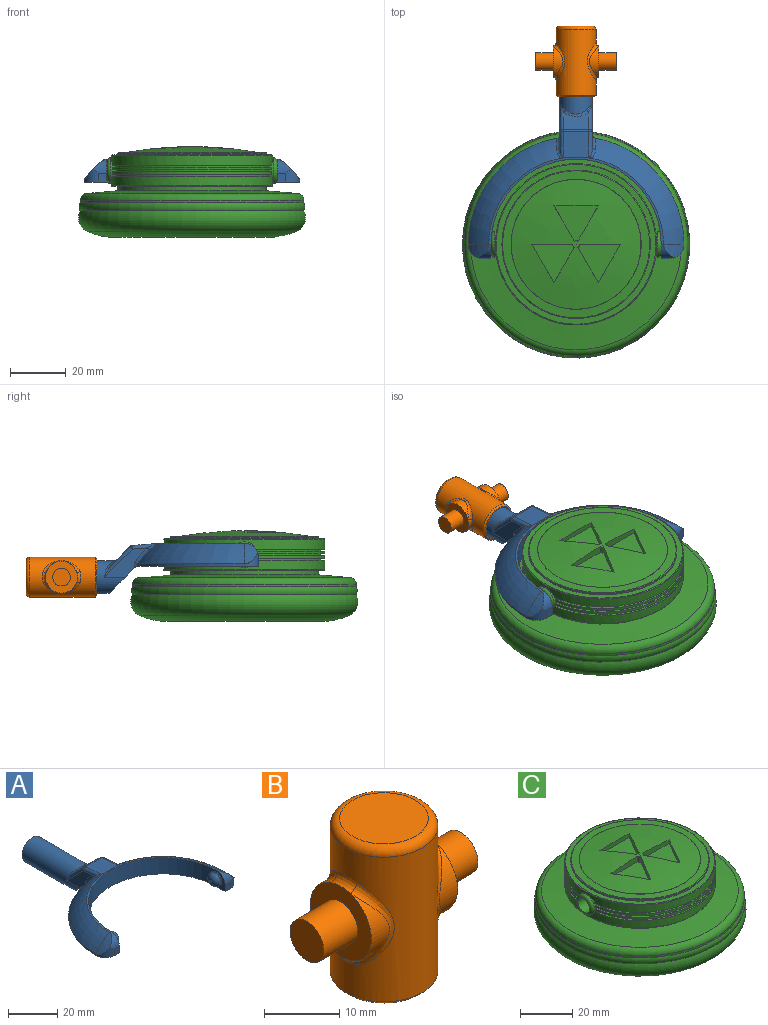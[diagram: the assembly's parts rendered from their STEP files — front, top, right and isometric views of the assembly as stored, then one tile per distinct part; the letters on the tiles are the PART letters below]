
ASSEMBLY  parts=3 mates=2
PART A: 48 faces, bbox 77.3x80.8x18.2 mm
  f0: plane 11.99x9.83mm, normal (0,-0.71,-0.71), area 141.5mm2, adj f1,f2,f9,f30,f43,f46
  f1: plane 15.39x10.49mm, normal (-1,0,0), area 63.5mm2, adj f0,f30,f32,f36,f46,f47
  f2: plane 15.39x10.49mm, normal (1,0,0), area 63.5mm2, adj f0,f30,f34,f39,f43,f44
  f3: plane 9.14x6.37mm, normal (0,0.71,0.71), area 67.6mm2, adj f35,f36,f39,f40
  f4: cylinder r=38.61mm len=37.99mm, axis (0,0,-1), area 42.6mm2, adj f6,f9,f17,f46,f47
  f5: torus R=19.3mm, axis (0,0,-1), area 507.8mm2, adj f10,f11,f12,f29,f42,f44
  f6: torus R=19.3mm, axis (0,0,-1), area 507.8mm2, adj f4,f11,f15,f28,f45,f47
  f7: cylinder r=30.48mm len=60.96mm, axis (0,0,-1), area 746.6mm2, adj f8,f9,f11,f14,f21,f24
  f8: plane 8.13x5.08mm, normal (-1,0,0), area 19.9mm2, adj f7,f9,f13,f19,f24
  f9: plane 77.22x43.73mm, normal (0,0,-1), area 956.2mm2, adj f0,f4,f7,f8,f10,f13,f14,f16
  f10: cylinder r=38.61mm len=37.99mm, axis (0,0,-1), area 42.6mm2, adj f5,f9,f20,f43,f44
  f11: plane 62.55x30.95mm, normal (0,0,1), area 75mm2, adj f5,f6,f7,f18,f19,f27
  f12: cylinder r=22.71mm len=7.33mm, axis (0,1,0), area 24.8mm2, adj f5,f19,f20
  f13: plane 3.05x3.05mm, normal (0,-1,0), area 9.3mm2, adj f8,f9,f19,f20
  f14: plane 8.13x5.08mm, normal (1,0,0), area 19.9mm2, adj f7,f9,f16,f18,f21
  f15: cylinder r=22.71mm len=7.33mm, axis (0,1,0), area 24.8mm2, adj f6,f17,f18
  f16: plane 3.05x3.05mm, normal (0,-1,0), area 9.3mm2, adj f9,f14,f17,f18
  f17: cylinder r=5.08mm len=5.08mm, axis (0,0,-1), area 21.9mm2, adj f4,f9,f15,f16,f18
  f18: cylinder r=5.08mm len=5.08mm, axis (-1,0,0), area 21.9mm2, adj f11,f14,f15,f16,f17
  f19: cylinder r=5.08mm len=5.08mm, axis (-1,0,0), area 21.9mm2, adj f8,f11,f12,f13,f20
  f20: cylinder r=5.08mm len=5.08mm, axis (0,0,-1), area 21.9mm2, adj f9,f10,f12,f13,f19
  f21: cylinder r=3.17mm len=6.35mm, axis (-1,0,0), area 12.7mm2, adj f7,f14,f23
  f22: plane 1.27x1.27mm, normal (1,0,0), area 1.3mm2, adj f23
  f23: torus R=0.64mm, axis (1,0,0), area 56.5mm2, adj f21,f22
  f24: cylinder r=3.17mm len=6.35mm, axis (1,0,0), area 12.7mm2, adj f7,f8,f26
  f25: plane 1.27x1.27mm, normal (-1,0,0), area 1.3mm2, adj f26
  f26: torus R=0.64mm, axis (-1,0,0), area 56.5mm2, adj f24,f25
  f27: plane 9.86x9.36mm, normal (0,0.09,1), area 85.6mm2, adj f11,f28,f29,f32,f34,f35,f42,f45
  f28: plane 1.04x0.17mm, normal (0,-1,0), area 0mm2, adj f6,f27,f45
  f29: plane 1.04x0.17mm, normal (0,-1,0), area 0mm2, adj f5,f27,f42
  f30: cylinder r=5.84mm len=33.01mm, axis (0,-1,0), area 1029.7mm2, adj f0,f1,f2,f31,f38,f40,f41
  f31: plane 11.68x11.68mm, normal (0,1,0), area 107.2mm2, adj f30
  f32: cylinder r=1.27mm len=9.13mm, axis (0,-1,0.09), area 14.4mm2, adj f1,f27,f33,f45
  f33: sphere r=1.27mm, area 1.5mm2, adj f32,f35,f36
  f34: cylinder r=1.27mm len=9.13mm, axis (0,1,-0.09), area 14.4mm2, adj f2,f27,f37,f42
  f35: cylinder r=1.27mm len=9.14mm, axis (-1,0,0), area 8.1mm2, adj f3,f27,f33,f37
  f36: cylinder r=1.27mm len=10.91mm, axis (0,-0.71,0.71), area 23.1mm2, adj f1,f3,f33,f38
  f37: sphere r=1.27mm, area 1.5mm2, adj f34,f35,f39
  f38: bspline ~4.55x2.75mm, area 2.3mm2, adj f30,f36,f40
  f39: cylinder r=1.27mm len=10.91mm, axis (0,0.71,-0.71), area 23.1mm2, adj f2,f3,f37,f41
  f40: bspline ~9.14x2.56mm, area 10.7mm2, adj f3,f30,f38,f41
  f41: bspline ~5.23x3.53mm, area 2.3mm2, adj f30,f39,f40
  f42: bspline ~4.62x3.14mm, area 5.2mm2, adj f5,f27,f29,f34,f44
  f43: cylinder r=1.27mm len=1.74mm, axis (0,0,-1), area 1.9mm2, adj f0,f2,f9,f10,f44
  f44: bspline ~8.6x7.86mm, area 11.9mm2, adj f2,f5,f10,f42,f43
  f45: bspline ~4.62x3.14mm, area 5.2mm2, adj f6,f27,f28,f32,f47
  f46: cylinder r=1.27mm len=1.74mm, axis (0,0,-1), area 1.9mm2, adj f0,f1,f4,f9,f47
  f47: bspline ~8.6x7.86mm, area 11.9mm2, adj f1,f4,f6,f45,f46
PART B: 25 faces, bbox 28.9x15.5x25.4 mm
  f0: cylinder r=5.71mm len=10.81mm, axis (-1,0,0), area 26.2mm2, adj f5,f15
  f1: cylinder r=5.71mm len=10.81mm, axis (-1,0,0), area 26.2mm2, adj f8,f11
  f2: cylinder r=7.14mm len=23.5mm, axis (0,0,-1), area 763.2mm2, adj f9,f10,f11,f12,f13,f14,f15,f16
  f3: plane 11.75x11.75mm, normal (0,0,1), area 108.4mm2, adj f17
  f4: plane 13.02x13.02mm, normal (0,0,-1), area 16.3mm2, adj f22,f24
  f5: plane 11.46x11.46mm, normal (1,0,0), area 70.9mm2, adj f0,f6,f13,f16,f18
  f6: cylinder r=5.71mm len=10.81mm, axis (-1,0,0), area 26.2mm2, adj f5,f14
  f7: cylinder r=5.71mm len=10.81mm, axis (-1,0,0), area 26.2mm2, adj f8,f10
  f8: plane 11.46x11.46mm, normal (-1,0,0), area 70.9mm2, adj f1,f7,f9,f12,f20
  f9: bspline ~4.64x1.73mm, area 6.5mm2, adj f2,f8,f10,f11
  f10: bspline ~13.62x4.91mm, area 20.7mm2, adj f2,f7,f9,f12
  f11: bspline ~13.6x4.87mm, area 20.7mm2, adj f1,f2,f9,f12
  f12: bspline ~4.64x1.73mm, area 6.5mm2, adj f2,f8,f10,f11
  f13: bspline ~4.64x1.73mm, area 6.5mm2, adj f2,f5,f14,f15
  f14: bspline ~13.62x4.91mm, area 20.7mm2, adj f2,f6,f13,f16
  f15: bspline ~13.6x4.87mm, area 20.7mm2, adj f0,f2,f13,f16
  f16: bspline ~4.64x1.73mm, area 6.5mm2, adj f2,f5,f14,f15
  f17: torus R=5.87mm, axis (0,0,1), area 83.8mm2, adj f2,f3
  f18: cylinder r=3.17mm len=6.35mm, axis (-1,0,0), area 126.7mm2, adj f5,f19
  f19: plane 6.35x6.35mm, normal (1,0,0), area 31.7mm2, adj f18
  f20: cylinder r=3.17mm len=6.35mm, axis (1,0,0), area 126.7mm2, adj f8,f21
  f21: plane 6.35x6.35mm, normal (-1,0,0), area 31.7mm2, adj f20
  f22: cylinder r=6.1mm len=22.86mm, axis (0,0,-1), area 875.6mm2, adj f4,f23
  f23: plane 12.19x12.19mm, normal (0,0,-1), area 116.7mm2, adj f22
  f24: cone r=7.14mm half-angle=45deg, axis (0,0,1), area 38.5mm2, adj f2,f4
PART C: 64 faces, bbox 96.2x96.2x32.5 mm
  f0: cylinder r=28.87mm len=57.73mm, axis (0,0,-1), area 590.8mm2, adj f1,f2,f54,f55,f60
  f1: plane 57.14x24.72mm, normal (0,0,1), area 102.1mm2, adj f0,f3,f54,f55
  f2: plane 57.14x24.72mm, normal (0,0,1), area 102.1mm2, adj f0,f4,f54,f55
  f3: cylinder r=27.6mm len=54.57mm, axis (0,0,-1), area 49.6mm2, adj f1,f6,f54,f55
  f4: cylinder r=27.6mm len=54.57mm, axis (0,0,-1), area 49.6mm2, adj f2,f5,f54,f55
  f5: plane 57.06x24.48mm, normal (0,0,-1), area 101.5mm2, adj f4,f8,f54,f55
  f6: plane 57.06x24.48mm, normal (0,0,-1), area 101.5mm2, adj f3,f7,f54,f55
  f7: cylinder r=28.87mm len=57.06mm, axis (0,0,-1), area 77.8mm2, adj f6,f9,f54,f55
  f8: cylinder r=28.87mm len=57.06mm, axis (0,0,-1), area 77.8mm2, adj f5,f10,f54,f55
  f9: plane 57.01x24.31mm, normal (0,0,1), area 101mm2, adj f7,f11,f54,f55
  f10: plane 57.01x24.31mm, normal (0,0,1), area 101mm2, adj f8,f12,f54,f55
  f11: cylinder r=27.6mm len=54.44mm, axis (0,0,-1), area 49.2mm2, adj f9,f13,f54,f55
  f12: cylinder r=27.6mm len=54.44mm, axis (0,0,-1), area 49.2mm2, adj f10,f14,f54,f55
  f13: plane 57.01x24.3mm, normal (0,0,-1), area 101mm2, adj f11,f15,f54,f55
  f14: plane 57.01x24.3mm, normal (0,0,-1), area 101mm2, adj f12,f16,f54,f55
  f15: cylinder r=28.87mm len=57.06mm, axis (0,0,-1), area 77.8mm2, adj f13,f22,f54,f55
  f16: cylinder r=28.87mm len=57.06mm, axis (0,0,-1), area 77.8mm2, adj f14,f21,f54,f55
  f17: cylinder r=27.6mm len=54.56mm, axis (0,0,-1), area 49.6mm2, adj f19,f22,f54,f55
  f18: cylinder r=27.6mm len=54.56mm, axis (0,0,-1), area 49.6mm2, adj f20,f21,f54,f55
  f19: plane 57.13x24.7mm, normal (0,0,-1), area 102mm2, adj f17,f23,f54,f55
  f20: plane 57.13x24.7mm, normal (0,0,-1), area 102mm2, adj f18,f23,f54,f55
  f21: plane 57.06x24.47mm, normal (0,0,1), area 101.4mm2, adj f16,f18,f54,f55
  f22: plane 57.06x24.47mm, normal (0,0,1), area 101.4mm2, adj f15,f17,f54,f55
  f23: cylinder r=28.87mm len=57.73mm, axis (0,0,-1), area 600.7mm2, adj f19,f20,f54,f55,f61
  f24: sphere r=135.39mm, area 1385.3mm2, adj f38,f39,f40,f41,f43,f44,f45,f46
  f25: plane 39.33x39.33mm, normal (0,0,-1), area 1214.6mm2, adj f26
  f26: torus R=20.12mm, axis (0,0,-1), area 1429.3mm2, adj f25,f27
  f27: torus R=27.74mm, axis (0,0,-1), area 3542.1mm2, adj f26,f28
  f28: torus R=35.36mm, axis (0,0,-1), area 2180.1mm2, adj f27,f29
  f29: torus R=37.35mm, axis (0,0,-1), area 734.6mm2, adj f28,f30
  f30: cylinder r=40.06mm len=80.11mm, axis (0,0,-1), area 213.3mm2, adj f29,f34
  f31: cone r=26.57mm half-angle=85deg, axis (0,0,-1), area 2265mm2, adj f32,f34
  f32: cylinder r=26.57mm len=53.14mm, axis (0,0,-1), area 265mm2, adj f31,f33
  f33: plane 57.23x57.23mm, normal (0,0,-1), area 354.5mm2, adj f32,f60
  f34: torus R=37.52mm, axis (0,0,1), area 928.6mm2, adj f30,f31
  f35: cone r=26.57mm half-angle=87deg, axis (0,0,-1), area 475.4mm2, adj f62,f63
  f36: cylinder r=26.57mm len=53.14mm, axis (0,0,-1), area 92.3mm2, adj f37,f62
  f37: plane 57.23x57.23mm, normal (0,0,1), area 354.5mm2, adj f36,f61
  f38: cylinder r=1.27mm len=2.53mm, axis (0,0,1), area 3.4mm2, adj f24,f39,f41,f42
  f39: plane 12.65x7.3mm, normal (0.87,0.5,0), area 32.2mm2, adj f24,f38,f40,f42
  f40: plane 13.75x7.94mm, normal (-0.87,0.5,0), area 28mm2, adj f24,f39,f41,f42
  f41: plane 14.61x2.53mm, normal (0,-1,0), area 32.2mm2, adj f24,f38,f40,f42
  f42: plane 15.24x13.75mm, normal (0,0,1), area 108.3mm2, adj f38,f39,f40,f41
  f43: cylinder r=1.27mm len=2.53mm, axis (0,0,1), area 3.4mm2, adj f24,f44,f46,f47
  f44: plane 14.61x2.53mm, normal (0,-1,0), area 32.2mm2, adj f24,f43,f45,f47
  f45: plane 13.75x7.94mm, normal (0.87,0.5,0), area 28mm2, adj f24,f44,f46,f47
  f46: plane 12.65x7.3mm, normal (-0.87,0.5,0), area 32.2mm2, adj f24,f43,f45,f47
  f47: plane 15.24x13.75mm, normal (0,0,1), area 108.3mm2, adj f43,f44,f45,f46
  f48: plane 15.88x1.84mm, normal (0,-1,0), area 28mm2, adj f24,f49,f51,f52
  f49: plane 12.65x7.3mm, normal (0.87,0.5,0), area 32.2mm2, adj f24,f48,f50,f52
  f50: cylinder r=1.27mm len=2.53mm, axis (0,0,1), area 3.4mm2, adj f24,f49,f51,f52
  f51: plane 12.65x7.3mm, normal (-0.87,0.5,0), area 32.2mm2, adj f24,f48,f50,f52
  f52: plane 15.88x12.65mm, normal (0,0,1), area 108.3mm2, adj f48,f49,f50,f51
  f53: plane 6.6x6.6mm, normal (1,0,0), area 2.6mm2, adj f58,f59
  f54: cylinder r=4.57mm len=9.14mm, axis (-1,0,0), area 20.2mm2, adj f0,f1,f2,f3,f4,f5,f6,f7
  f55: cylinder r=4.57mm len=9.14mm, axis (-1,0,0), area 20.2mm2, adj f0,f1,f2,f3,f4,f5,f6,f7
  f56: plane 6.6x6.6mm, normal (-1,0,0), area 2.6mm2, adj f57,f59
  f57: torus R=3.3mm, axis (1,0,0), area 51.5mm2, adj f55,f56
  f58: torus R=3.3mm, axis (1,0,0), area 51.5mm2, adj f53,f54
  f59: cylinder r=3.17mm len=60.96mm, axis (1,0,0), area 1216.1mm2, adj f53,f56
  f60: torus R=28.61mm, axis (0,0,1), area 72.1mm2, adj f0,f33
  f61: torus R=28.61mm, axis (0,0,-1), area 72.1mm2, adj f23,f37
  f62: torus R=26.31mm, axis (0,0,1), area 64.2mm2, adj f35,f36
  f63: torus R=23.29mm, axis (0,0,1), area 4.5mm2, adj f24,f35
PLACE A t=(32.34,27.52,20.85)mm
PLACE B rot(axis=(-1,0,0),90deg) t=(32.34,80.3,16.88)mm
PLACE C t=(32.34,27.52,33.52)mm
MATE revolute A.f24 <-> C.f54  axis (-1,0,0) through (62.82,27.52,24.92)mm
MATE revolute B.f2 <-> A.f30  axis (0,-1,0) through (32.34,103.16,16.88)mm
